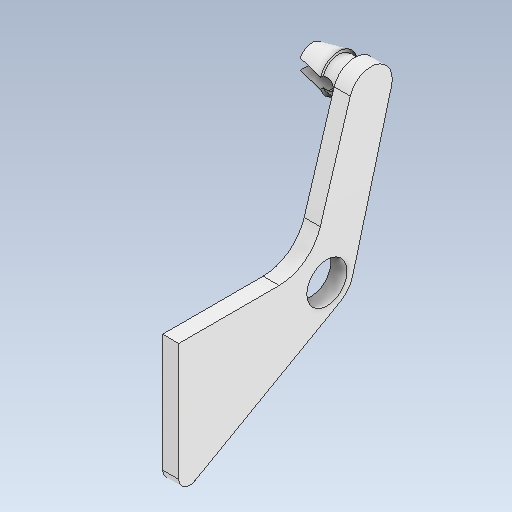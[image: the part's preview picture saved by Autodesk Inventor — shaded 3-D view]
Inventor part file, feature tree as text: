
AUTODESK INVENTOR PART (.ipt)
format: ipt  version: 2021 (Build 250183000, 183)  size: 188,416 bytes
history: native  units: mm
features: sketch x3, extrude x2, fillet x2, plane x2, revolve x1
ambient origin geometry x8: Origin, YZ Plane, XZ Plane, XY Plane, X Axis, Y Axis, Z Axis, Center Point
bodies: Body1 (feature_tree)
feature tree (10):
  extrude  "Extrusión2"  Depth=28.0mm
  fillet  "Empalme1"  Radius=4.0mm
  plane  "Plano de trabajo3"
  revolve  "Revolución1"  [1 undecoded]
  plane  "Plano de trabajo4"
  extrude  "Extrusión3"  Depth=1.0mm
  fillet  "Empalme2"  Radius=3.0mm
  sketch  "Boceto4"  dims[d18=25.2mm d20=28.0mm d22=4.0mm]
  sketch  "Boceto5"  dims[d23=20.0mm d24=2.4mm]
  sketch  "Boceto6"  dims[d25=2.0mm d26=7.5mm d27=3.0mm d28=0.0mm d29=8.0mm d30=-8.186408mm d31=26.776533mm d32=1.5mm d33=3.0mm d34=3.0mm d35=0.5mm d36=5.0mm d37=3.5mm d38=2.373201mm d39=90.0deg d40=3.5mm d41=2.0mm d42=14.0mm d43=0.0mm d44=18.675023mm d45=2.4mm d47=1.0mm]
note: 1 required parameter value undecoded (feature->parameter linkage not recoverable at this tier; creation-order binding heuristic only, values carry confidence <= 0.55)
